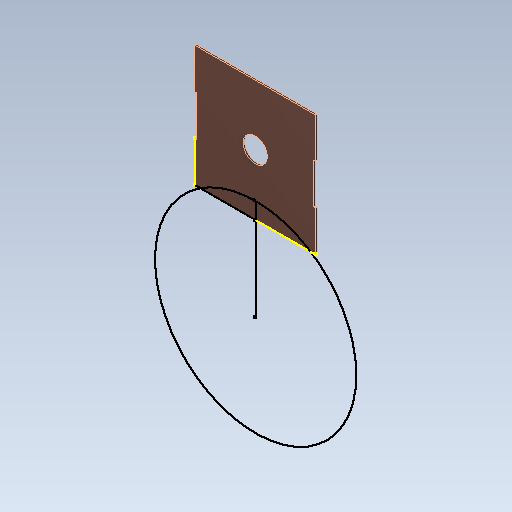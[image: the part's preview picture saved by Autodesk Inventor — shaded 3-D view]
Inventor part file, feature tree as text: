
AUTODESK INVENTOR PART (.ipt)
format: ipt  version: 2021 (Build 250183000, 183)  size: 112,128 bytes
history: native  units: mm
features: other x1, sketch x1
ambient origin geometry x8: Origin, YZ Plane, XZ Plane, XY Plane, X Axis, Y Axis, Z Axis, Center Point
bodies: Solid2 (feature_tree), Solid1 (feature_tree)
feature tree (2):
  other  "Repaired Geometry1"
  sketch  "Sketch3"
